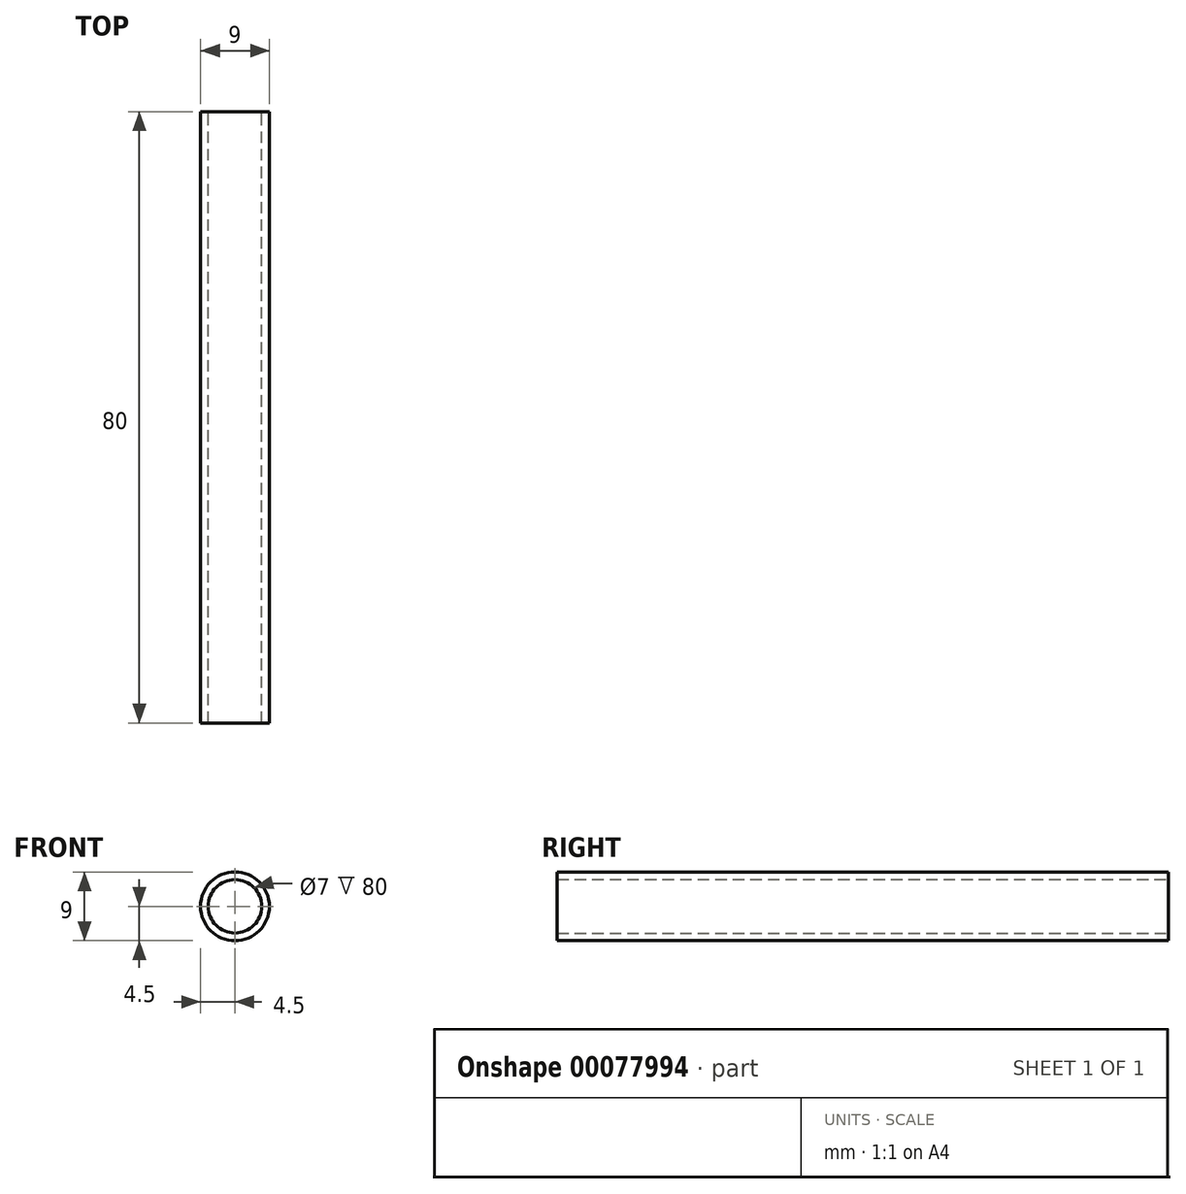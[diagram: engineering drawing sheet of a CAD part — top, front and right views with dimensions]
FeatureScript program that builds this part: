
annotation { "Feature Type Name" : "Feature", "Feature Type Description" : "" }
export const myFeature = defineFeature(function(context is Context, id is Id, definition is map)
    precondition{}
    {
        {
            var Q0;
            Q0=qCreatedBy(makeId("Front.planeOp"),FACE);
            var sketch = newSketch(context, id + "F0", { "sketchPlane" : qUnion([Q0])});
            skCircle(sketch, "E0", {"center": v(0, 0) * mm, "radius": 3.5 * mm});
            skCircle(sketch, "E1", {"center": v(0, 0) * mm, "radius": 4.5 * mm});
            skSolve(sketch);
        }
        {
            var Q0;
            Q0=qSketchRegion(id+"F0",true);
            extrude(context, id + "F1", {"entities" : qUnion([Q0]), "depth" : 80 * mm});
        }
    });
